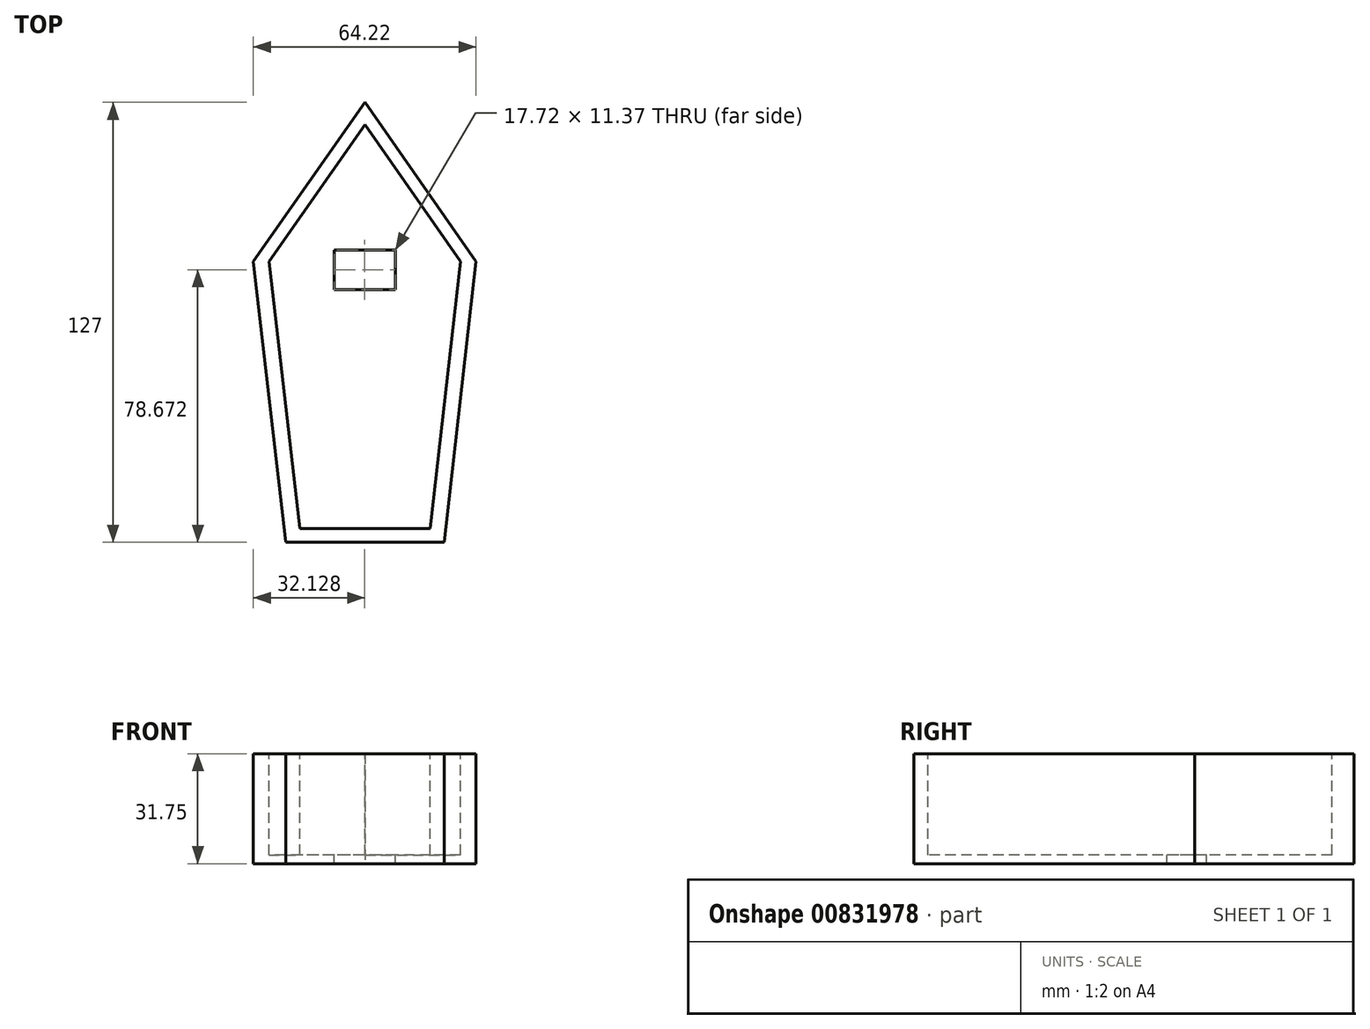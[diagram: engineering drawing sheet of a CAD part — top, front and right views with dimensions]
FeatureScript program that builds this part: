
annotation { "Feature Type Name" : "Feature", "Feature Type Description" : "" }
export const myFeature = defineFeature(function(context is Context, id is Id, definition is map)
    precondition{}
    {
        {
            var Q0;
            Q0=qCreatedBy(makeId("Top.planeOp"),FACE);
            var sketch = newSketch(context, id + "F0", { "sketchPlane" : qUnion([Q0])});
            skLineSegment(sketch, "E0.bottom", {"start": v(-25.06, 48.98) * mm, "end": v(20.66, 48.98) * mm});
            skLineSegment(sketch, "E0.top", {"start": v(-25.06, -45) * mm, "end": v(20.66, -45) * mm});
            skLineSegment(sketch, "E0.left", {"start": v(-25.06, 48.98) * mm, "end": v(-25.06, -45) * mm});
            skLineSegment(sketch, "E0.right", {"start": v(20.66, 48.98) * mm, "end": v(20.66, -45) * mm});
            skLineSegment(sketch, "E1", {"start": v(-2.2, -45) * mm, "end": v(-2.2, 82) * mm});
            skLineSegment(sketch, "E2", {"start": v(-2.2, 82) * mm, "end": v(-34.44, 36.02) * mm});
            skLineSegment(sketch, "E3", {"start": v(-34.44, 36.02) * mm, "end": v(-25.06, -45) * mm});
            skLineSegment(sketch, "E4", {"start": v(-2.2, 82) * mm, "end": v(29.78, 36.02) * mm});
            skLineSegment(sketch, "E5", {"start": v(29.78, 36.02) * mm, "end": v(20.66, -45) * mm});
            skSolve(sketch);
        }
        {
            var Q0;
            Q0=qSketchRegion(id+"F0",true);
            extrude(context, id + "F1", {"entities" : qUnion([Q0]), "depth" : 31.75 * mm, "offsetDistance" : 25.4 * mm});
        }
        {
            var Q0;
            Q0=makeQuery(id+"F1.opExtrude","CAP_FACE",FACE,{"disambiguationData":[OSD([sQuery(id+"F0.wireOp",EDGE,"E0.top"),sQuery(id+"F0.wireOp",EDGE,"E2"),sQuery(id+"F0.wireOp",EDGE,"E3"),sQuery(id+"F0.wireOp",EDGE,"E4"),sQuery(id+"F0.wireOp",EDGE,"E5")])],"isStart":false});
            var sketch = newSketch(context, id + "F2", { "sketchPlane" : qUnion([Q0])});
            skLineSegment(sketch, "E6", {"start": v(-2.2, 82) * mm, "end": v(-2.2, 75.55) * mm});
            skLineSegment(sketch, "E7", {"start": v(-2.2, 75.55) * mm, "end": v(-29.92, 36.02) * mm});
            skLineSegment(sketch, "E8", {"start": v(-29.92, 36.02) * mm, "end": v(-21, -41.01) * mm});
            skLineSegment(sketch, "E9", {"start": v(-2.2, 75.55) * mm, "end": v(25.3, 36.02) * mm});
            skLineSegment(sketch, "E10", {"start": v(25.3, 36.02) * mm, "end": v(16.62, -41.01) * mm});
            skLineSegment(sketch, "E11", {"start": v(16.62, -41.01) * mm, "end": v(-21, -41.01) * mm});
            skSolve(sketch);
        }
        {
            var Q0;
            Q0=makeQuery(id+"F2.imprint","IMPRINT",FACE,{"disambiguationData":[TD([[makeQuery(id+"F2.imprint","IMPRINT",EDGE,{"derivedFrom":sQuery(id+"F2.wireOp",EDGE,"E7")}),1.0]])]});
            extrude(context, id + "F3", {"entities" : qUnion([Q0]), "operationType" : NewBodyOperationType.REMOVE, "oppositeDirection" : true, "depth" : 29.2 * mm, "offsetDistance" : 25.4 * mm});
        }
        {
            var Q0;
            Q0=makeQuery(id+"F3.boolean.opBoolean","COPY",FACE,{"derivedFrom":makeQuery(id+"F3.opExtrude","CAP_FACE",FACE,{"disambiguationData":[OSD([sQuery(id+"F2.wireOp",EDGE,"E7"),sQuery(id+"F2.wireOp",EDGE,"E8"),sQuery(id+"F2.wireOp",EDGE,"E9"),sQuery(id+"F2.wireOp",EDGE,"E10"),sQuery(id+"F2.wireOp",EDGE,"E11")])],"isStart":false})});
            var sketch = newSketch(context, id + "F4", { "sketchPlane" : qUnion([Q0])});
            skLineSegment(sketch, "E12", {"start": v(-2.2, 75.55) * mm, "end": v(-2.2, 39.36) * mm});
            skLineSegment(sketch, "E13", {"start": v(-2.2, 39.36) * mm, "end": v(-11.17, 39.36) * mm});
            skLineSegment(sketch, "E14.bottom", {"start": v(-11.17, 39.36) * mm, "end": v(6.55, 39.36) * mm});
            skLineSegment(sketch, "E14.top", {"start": v(-11.17, 27.98) * mm, "end": v(6.55, 27.98) * mm});
            skLineSegment(sketch, "E14.left", {"start": v(-11.17, 39.36) * mm, "end": v(-11.17, 27.98) * mm});
            skLineSegment(sketch, "E14.right", {"start": v(6.55, 39.36) * mm, "end": v(6.55, 27.98) * mm});
            skSolve(sketch);
        }
        {
            var Q0;
            Q0=makeQuery(id+"F4.imprint","IMPRINT",FACE,{"disambiguationData":[TD([[makeQuery(id+"F4.imprint","IMPRINT",EDGE,{"derivedFrom":sQuery(id+"F4.wireOp",EDGE,"E14.top")}),1.0]])]});
            extrude(context, id + "F5", {"entities" : qUnion([Q0]), "operationType" : NewBodyOperationType.REMOVE, "oppositeDirection" : true, "depth" : 25.4 * mm, "offsetDistance" : 25.4 * mm});
        }
    });
